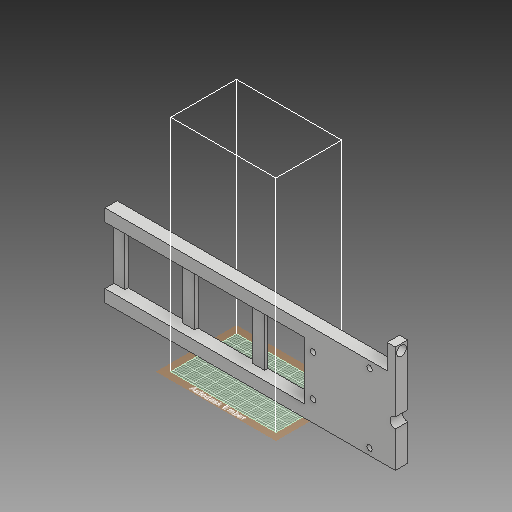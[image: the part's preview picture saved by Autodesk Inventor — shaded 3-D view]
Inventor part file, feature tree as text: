
AUTODESK INVENTOR PART (.ipt)
format: ipt  version: 2018 (Build 220112000, 112)  size: 869,376 bytes
history: native  units: mm
features: sketch x56, extrude x43, fillet x12, hole x8
ambient origin geometry x8: Origin, YZ Plane, XZ Plane, XY Plane, X Axis, Y Axis, Z Axis, Center Point
bodies: Solid1 (feature_tree)
feature tree (119):
  extrude  "Extrusion1"  Depth=50.0mm
  hole  "Hole1"  [1 undecoded]
  hole  "Hole2"  [1 undecoded]
  extrude  "Extrusion2"  Depth=25.0mm
  extrude  "Extrusion3"  Depth=25.0mm
  extrude  "Extrusion4"  Depth=5.0mm
  sketch  "Sketch7"  dims[d25=10.0mm d26=5.0mm]
  extrude  "Extrusion5"  Depth=5.0mm
  extrude  "Extrusion6"  Depth=35.0mm
  extrude  "Extrusion7"  Depth=35.0mm
  extrude  "Extrusion8"  Depth=35.0mm
  extrude  "Extrusion9"  Depth=2.0mm TaperAngle=0.0deg
  extrude  "Extrusion10"  Depth=7.5mm TaperAngle=0.0deg
  extrude  "Extrusion11"  Depth=10.0mm
  extrude  "Extrusion12"  Depth=7.5mm
  fillet  "Fillet1"  Radius=7.5mm
  fillet  "Fillet2"  Radius=25.0mm
  fillet  "Fillet3"  Radius=3.0mm
  fillet  "Fillet4"  Radius=3.2mm
  fillet  "Fillet5"  Radius=2.1mm
  fillet  "Fillet6"  Radius=5.5mm
  extrude  "Extrusion13"  Depth=92.5mm TaperAngle=0.0deg
  sketch  "Sketch17"  dims[d58=4.25mm d59=241.0mm d60=0.0mm]
  hole  "Hole3"  [1 undecoded]
  hole  "Hole4"  [1 undecoded]
  extrude  "Extrusion14"  Depth=5.0mm
  extrude  "Extrusion15"  Depth=2.5mm TaperAngle=0.0deg
  extrude  "Extrusion16"  Depth=6.35mm
  extrude  "Extrusion17"  Depth=2.5mm
  extrude  "Extrusion18"  Depth=14.55mm TaperAngle=0.0deg
  extrude  "Extrusion19"  Depth=0.1mm
  extrude  "Extrusion20"  Depth=3.25mm
  extrude  "Extrusion21"  Depth=3.25mm
  hole  "Hole5"  [1 undecoded]
  extrude  "Extrusion22"  Depth=2.0mm
  extrude  "Extrusion23"  Depth=15.0mm
  extrude  "Extrusion24"  Depth=10.0mm TaperAngle=0.0deg
  hole  "Hole6"  [1 undecoded]
  extrude  "Extrusion25"  Depth=100.0mm TaperAngle=0.0deg
  extrude  "Extrusion26"  Depth=2.0mm TaperAngle=0.0deg
  extrude  "Extrusion27"  Depth=3.3mm
  extrude  "Extrusion28"  Depth=3.3mm
  hole  "Hole7"  [1 undecoded]
  extrude  "Extrusion29"  Depth=2.0mm
  extrude  "Extrusion30"  Depth=17.0mm
  hole  "Hole8"  [1 undecoded]
  extrude  "Extrusion31"  Depth=21.0mm
  extrude  "Extrusion32"  Depth=10.0mm
  fillet  "Fillet7"  Radius=3.3mm
  fillet  "Fillet8"  Radius=10.0mm
  extrude  "Extrusion33"  Depth=5.0mm
  extrude  "Extrusion34"  Depth=5.0mm
  sketch  "Sketch45"  dims[d149=10.0mm d150=17.5mm d151=0.0mm]
  sketch  "Sketch46"  dims[d152=5.0mm]
  extrude  "Extrusion35"  Depth=10.0mm TaperAngle=0.0deg
  extrude  "Extrusion36"  Depth=2.0mm TaperAngle=0.0deg
  extrude  "Extrusion37"  Depth=3.75mm
  extrude  "Extrusion38"  Depth=3.75mm
  extrude  "Extrusion39"  Depth=10.0mm TaperAngle=0.0deg
  extrude  "Extrusion40"  Depth=2.0mm TaperAngle=0.0deg
  fillet  "Fillet9"  Radius=5.0mm
  fillet  "Fillet10"  Radius=15.0mm
  fillet  "Fillet11"  Radius=7.5mm
  fillet  "Fillet12"  Radius=17.5mm
  extrude  "Extrusion41"  Depth=47.5mm
  extrude  "Extrusion42"  Depth=5.0mm
  sketch  "Sketch55"  dims[d200=20.0mm d203=5.0mm]
  extrude  "Extrusion43"  Depth=29.0mm
  sketch  "Sketch1"  dims[d0=50.0mm d1=50.0mm]
  sketch  "Sketch2"  dims[d2=240.0mm d3=7.5mm]
  sketch  "Sketch3"  dims[d4=7.5mm d5=7.5mm d6=0.0mm]
  sketch  "Sketch4"  dims[d7=6.35mm d8=6.0mm d9=4.0mm d10=2.0mm d11=90.0deg d12=8.0mm d13=20.594885mm d14=25.0mm]
  sketch  "Sketch5"  dims[d15=3.3mm d16=6.0mm d17=4.0mm d18=2.0mm d19=90.0deg d20=8.0mm d21=20.594885mm d22=25.0mm]
  sketch  "Sketch6"  dims[d23=180.0deg d24=5.0mm]
  sketch  "Sketch8"  dims[d27=17.5mm d28=0.0mm d30=35.0mm]
  sketch  "Sketch9"  dims[d31=35.0mm d32=35.0mm]
  sketch  "Sketch10"  dims[d33=35.0mm d34=35.0mm]
  sketch  "Sketch11"  dims[d35=35.0mm d36=2.0mm d37=0.0mm]
  sketch  "Sketch12"  dims[d38=10.0mm d39=7.5mm d40=0.0mm]
  sketch  "Sketch13"  dims[d41=100.0mm d42=10.0mm]
  sketch  "Sketch14"  dims[d43=7.5mm d44=0.0mm d45=7.5mm d46=7.5mm d47=25.0mm d48=0.0mm d49=3.0mm d50=3.2mm d51=2.1mm d52=5.5mm]
  sketch  "Sketch15"  dims[d53=3.3mm d54=92.5mm d55=0.0mm]
  sketch  "Sketch16"  dims[d56=5.5mm d57=3.3mm]
  sketch  "Sketch18"  dims[d61=4.44mm d62=5.0mm]
  sketch  "Sketch19"  dims[d63=2.5mm d64=91.25mm d65=0.0mm]
  sketch  "Sketch20"  dims[d66=30.0mm d67=6.35mm]
  sketch  "Sketch21"  dims[d68=3.8mm d69=0.0mm d70=2.5mm]
  sketch  "Sketch22"  dims[d71=14.55mm d72=0.0mm d73=14.55mm d74=0.0mm]
  sketch  "Sketch23"  dims[d75=0.1mm d76=0.1mm]
  sketch  "Sketch24"  dims[d77=3.25mm d78=3.25mm]
  sketch  "Sketch25"  dims[d79=3.25mm d80=3.25mm]
  sketch  "Sketch26"  dims[d81=35.0mm d82=10.0mm]
  sketch  "Sketch27"  dims[d83=2.0mm d84=0.0mm d85=3.6mm]
  sketch  "Sketch28"  dims[d86=3.6mm]
  sketch  "Sketch29"  dims[d87=3.3mm d88=6.0mm d89=4.0mm d90=2.0mm d91=90.0deg d92=15.0mm d93=20.594885mm]
  sketch  "Sketch30"  dims[d94=3.3mm d95=6.0mm d96=4.0mm d97=2.0mm d98=90.0deg d99=15.0mm d100=20.594885mm d101=6.0mm]
  sketch  "Sketch31"  dims[d102=20.0mm d103=0.0mm d104=10.0mm d105=0.0mm]
  sketch  "Sketch32"  dims[d106=2.0mm d107=0.0mm d108=4.0mm]
  sketch  "Sketch33"  dims[d109=100.0mm d110=0.0mm d111=100.0mm d112=0.0mm]
  sketch  "Sketch34"  dims[d113=5.0mm d114=2.0mm d115=0.0mm]
  sketch  "Sketch35"  dims[d116=3.3mm d117=3.3mm]
  sketch  "Sketch36"  dims[d118=3.3mm d119=3.3mm]
  sketch  "Sketch37"  dims[d120=2.0mm d121=0.0mm d122=5.5mm d123=0.0mm]
  sketch  "Sketch38"  dims[d124=3.3mm d125=6.0mm d126=4.0mm d127=2.0mm d128=90.0deg d129=8.0mm d130=20.594885mm d131=42.0mm]
  sketch  "Sketch39"  dims[d132=17.0mm d133=21.0mm]
  sketch  "Sketch40"  dims[d135=8.5mm d136=15.825mm]
  sketch  "Sketch41"  dims[d137=3.5mm d138=21.0mm]
  sketch  "Sketch42"  dims[d139=3.3mm d140=3.3mm d141=3.3mm d142=10.0mm d143=0.0mm]
  sketch  "Sketch43"  dims[d144=7.5mm d145=0.0mm d146=5.0mm]
  sketch  "Sketch44"  dims[d147=10.0mm d148=5.0mm]
  sketch  "Sketch47"  dims[d153=7.0mm d154=6.0mm d155=4.0mm d156=2.0mm d157=90.0deg d158=8.0mm d159=20.594885mm d160=17.5mm d161=0.0mm]
  sketch  "Sketch48"  dims[d162=170.5mm d163=0.0mm d164=3.75mm]
  sketch  "Sketch49"  dims[d165=3.75mm d166=3.75mm]
  sketch  "Sketch50"  dims[d167=3.75mm d168=10.0mm d169=0.0mm]
  sketch  "Sketch51"  dims[d170=100.0mm d171=0.0mm]
  sketch  "Sketch52"  dims[d172=5.0mm d173=6.0mm d174=4.0mm d175=2.0mm d176=90.0deg d177=15.0mm d178=0.0mm d179=2.0mm d180=0.0mm d181=5.0mm d182=15.0mm d183=0.0mm d184=7.5mm]
  sketch  "Sketch53"  dims[d185=6.0mm d186=6.0mm d187=4.0mm d188=2.0mm d189=90.0deg d190=15.0mm d191=0.0mm d192=17.5mm d193=0.0mm]
  sketch  "Sketch54"  dims[d194=23.75mm d195=47.5mm]
  sketch  "Sketch56"  dims[d204=5.0mm d205=29.0mm d206=29.0mm d207=7.5mm d208=0.0mm d209=4.0mm d210=4.0mm d211=2.0mm d212=0.0mm d213=12.0mm d214=2.0mm d215=0.0mm d216=7.5mm d217=7.5mm d218=20.0mm d219=0.0mm d220=20.0mm d221=3.3mm d222=20.0mm d223=0.0mm d224=4.0mm d225=4.0mm d226=10.0mm d227=0.0mm d228=3.0mm d229=5.5mm d230=0.0mm d231=10.0mm d232=0.0mm d233=74.724mm d234=74.724mm d235=85.515mm d236=5.0mm d237=5.0mm d238=85.515mm d239=5.0mm d240=85.515mm d241=5.0mm d242=2.0mm d243=0.0mm d244=2.0mm d245=2.0mm d246=2.0mm d247=2.0mm d248=10.0mm d249=2.0mm d250=0.0mm d251=1.0mm d252=0.0mm d253=20.0mm d254=1.0mm d255=0.0mm]
note: 8 required parameter values undecoded (feature->parameter linkage not recoverable at this tier; creation-order binding heuristic only, values carry confidence <= 0.55)
